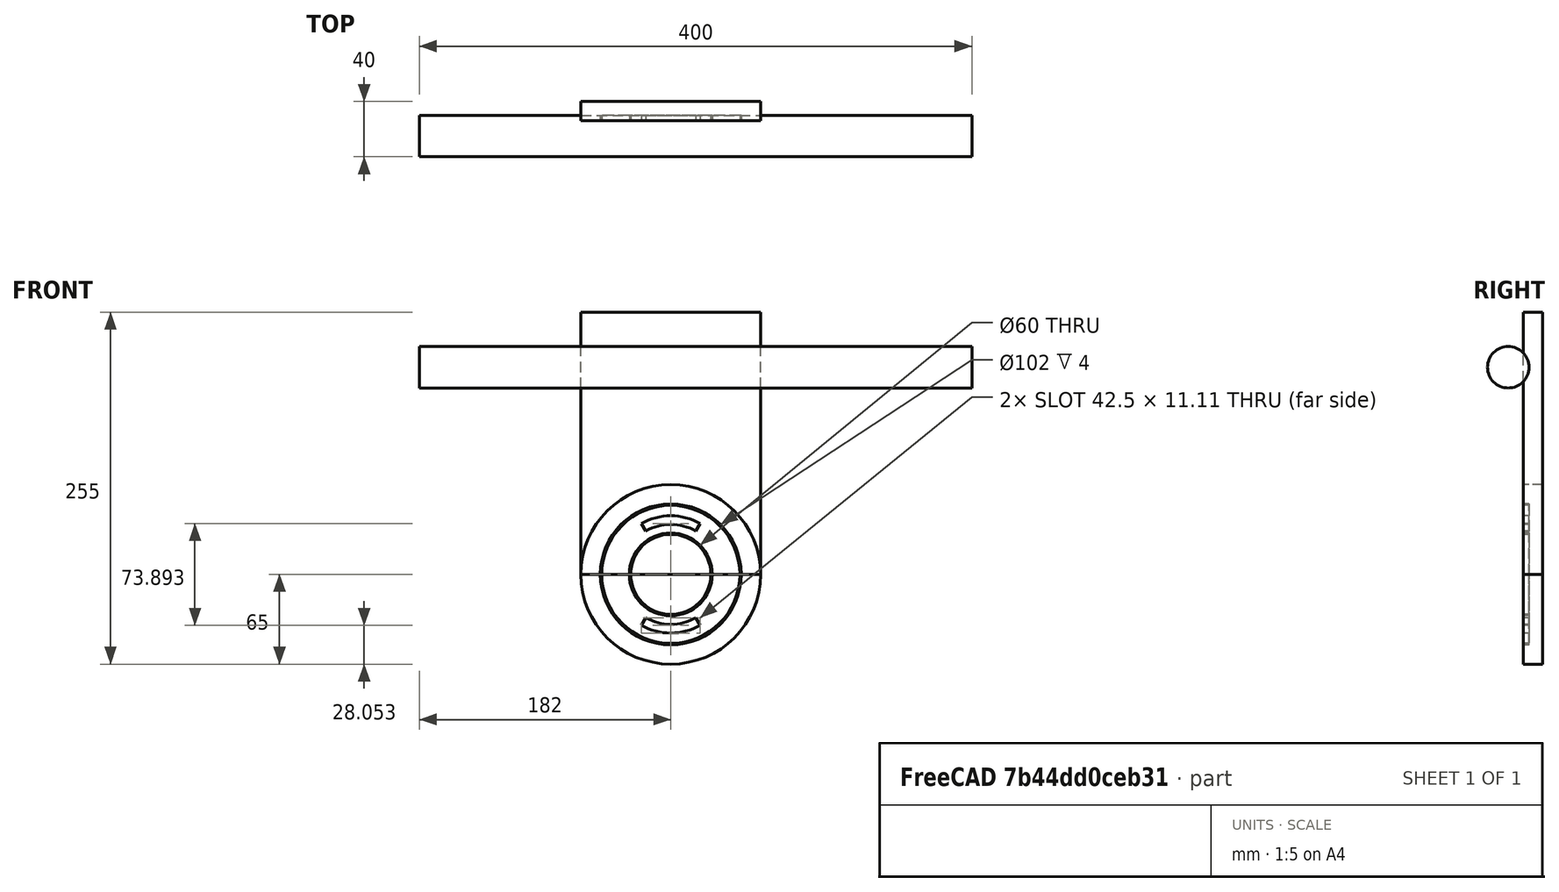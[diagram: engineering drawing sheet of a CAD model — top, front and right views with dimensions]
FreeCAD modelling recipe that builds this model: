
FCSTD DOCUMENT  (FreeCAD 0.19R24276 (Git))
Label: cameraMountMidPiece
License: All rights reserved
LicenseURL: http://en.wikipedia.org/wiki/All_rights_reserved
objects: Part::Cylinder×9, Part::Cut×4, Part::MultiFuse×2, Part::FeaturePython×1, Part::Box×1
note: 17 computed .brp shape members not serialized (recipe doc carries the construction recipe); baked Part::Feature solids carry a one-line shape summary decoded from their .brp

FEATURE [Part::Cylinder] Cylinder  label="hor"
  Angle = 360
  AttacherType = Attacher::AttachEngine3D
  Height = 400
  Placement = pos=(0,0,150) rot=(0.707107,0,0.707107;3.14159rad)
  Radius = 15
FEATURE [Part::Cylinder] Cylinder001  label="Cylinder"
  Angle = 360
  AttacherType = Attacher::AttachEngine3D
  Height = 4
  Placement = pos=(182,-19,-4.2e-15) rot=(-1,0,0;4.71239rad)
  Radius = 50
FEATURE [Part::Cylinder] Cylinder002
  Angle = 360
  AttacherType = Attacher::AttachEngine3D
  Height = 4.5
  Placement = pos=(182,-19,-4e-15) rot=(1,0,0;1.5708rad)
  Radius = 30
FEATURE [Part::Cut] Cut  label="cameraPlate"
  Base = -> Cylinder001
  Tool = -> Cylinder002
FEATURE [Part::Cylinder] Cylinder003
  Angle = 60
  AttacherType = Attacher::AttachEngine3D
  Height = 4.5
  Placement = pos=(182,-19,-4e-15) rot=(-0.377964,-0.654654,0.654654;3.86433rad)
  Radius = 36.25
FEATURE [Part::Cylinder] Cylinder004
  Angle = 60
  AttacherType = Attacher::AttachEngine3D
  Height = 4.5
  Placement = pos=(182,-19,-4e-15) rot=(-0.377964,-0.654654,0.654654;3.86433rad)
  Radius = 42.5
FEATURE [Part::Cylinder] Cylinder005
  Angle = 60
  AttacherType = Attacher::AttachEngine3D
  Height = 4.5
  Placement = pos=(182,-19,-4e-15) rot=(0.774597,-0.447214,0.447214;1.82348rad)
  Radius = 42.5
FEATURE [Part::Cylinder] Cylinder006
  Angle = 60
  AttacherType = Attacher::AttachEngine3D
  Height = 4.5
  Placement = pos=(182,-19,-4e-15) rot=(0.774597,-0.447214,0.447214;1.82348rad)
  Radius = 36.25
FEATURE [Part::Cut] Cut001
  Base = -> Cylinder004
  Tool = -> Cylinder003
FEATURE [Part::Cut] Cut002
  Base = -> Cylinder005
  Tool = -> Cylinder006
FEATURE [Part::MultiFuse] Fusion
  Shapes = -> [Cut002,Cut001]
FEATURE [Part::Cut] Cut003  label="cameraPlate001"
  Base = -> Cut
  Placement = pos=(0,34,0) rot=(0,0,1;0rad)
  Tool = -> Fusion
FEATURE [Part::Cylinder] Cylinder007
  Angle = 360
  AttacherType = Attacher::AttachEngine3D
  Height = 10
  Placement = pos=(182,25,-1.38e-14) rot=(1,0,0;1.5708rad)
  Radius = 65
FEATURE [Part::Cylinder] Cylinder008
  Angle = 360
  AttacherType = Attacher::AttachEngine3D
  Height = 4
  Placement = pos=(182,15,-1.14e-14) rot=(1,0,0;1.5708rad)
  Radius = 29
FEATURE [Part::FeaturePython] Tube  # WARN: FeaturePython — macro-defined, semantics opaque (R4)
  AttacherType = Attacher::AttachEngine3D
  Height = 4
  InnerRadius = 51
  OuterRadius = 65
  Placement = pos=(182,15,-3.3e-15) rot=(1,0,0;1.5708rad)
FEATURE [Part::MultiFuse] Fusion001  label="camBack"
  Shapes = -> [Tube,Cylinder007,Cylinder008]
FEATURE [Part::Box] Box  label="camAddOns"
  AttacherType = Attacher::AttachEngine3D
  Height = 14
  Length = 130
  Placement = pos=(117,25,5.6e-15) rot=(-1,0,0;4.71239rad)
  Width = 190
